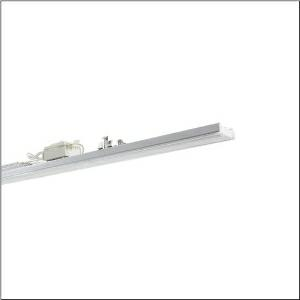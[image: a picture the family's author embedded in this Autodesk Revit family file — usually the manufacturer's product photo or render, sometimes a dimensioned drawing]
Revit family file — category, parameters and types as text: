
# Revit family: licross_r__21_recessed_ho_51te11vn4c5sd_75f8
name_source: partatom
category: Lighting Fixtures
units: mm (PartAtom-declared; Revit-internal decimal feet)

## family parameters
Cut with Voids When Loaded = No
Host = Face
Light Source = No
Part Type = Normal
Room Calculation Point = No
Round Connector Dimension = Use Diameter
Shared = No

## types (1)
- --- (1 x LED, 2050 lm, 12.3 W, 4000K)
    Apparent Load = 12 VA
    CIE Flux Codes = 84 94 98 99 100
    Color Rendering = 80
    Color Temperature = 4000K
    Default Elevation = 1800 mm
    Description = Licross® 21 Recessed HO, luminaire insert, of sheet steel, galvanised, coil coated, white, length: 1.500mm, width: 66mm, height: 67mm, LED rated luminous flux: 12.960lm, light colour: 840, control gear: DALI 2, CLO (for two DALI lines), with plug, 6-pole, with phase selection, mains connection: 220..240V, AC/DC, 0/50..60Hz, start of lifetime: 71W, end of service life: 77W, internal wiring halogen-free, for central battery installations according to DIN EN 60598-2-22, for emergency light function, without changeover relay, primary optical cover: cover, of PMMA, light emission: direct distribution, primary light characteristic: symmetric, protection rating (complete): IP54, insulation class (complete): insulation class I (protective earthing), certification: CE, ENEC, VDE, UKCA, protection symbol: D if used in an environment with non-conductive dust loads with corresponding accessories, impact resistance: IK06, permissible ambient temperature for indoor applications: -25..+35°C, standard: EN 60598-2-22, corresponds to IFS (International Featured Standards) requirements for safety and quality in the food industry, reducing of maximum allowable ambient temperature of 5°C with ceiling mounting, LABS conformity tested according to VDMA 24364:2018-05, packaging unit: 1 piece
    Height = 58 mm
    Lamp = 1 x LED
    Lamp Light Flux = 2050 lm
    Lamp Power = 12.3 W
    Lamp count = 1
    Length = 1500 mm
    Luminous efficacy = 167 lm/W
    Manufacturer = Siteco
    ModVariant = No
    Model = 51TE11VN4C5SD
    Mounting Place = Ceiling
    Mounting Type = Pendant
    Number of Poles = 1
    OnlyDefault = Yes
    Power Factor = 1
    Product Name = Licross® 21 Recessed HO
    Product group = luminaire insert | ceiling pendant
    ProductGroupID = 902
    Protection Class = Protection class I
    Protection Degree = IP 54
    RLX_Detail_Level = 1
    RLX_Emergency_Light_Flux = 0 lm
    RLX_Emergency_Type = 0
    RLX_Emergency_Type_DB = No
    RlxData = <blob elided: 25425 chars, md5=5d87726e>
    Socket = socket
    Standby Power = 0 W
    System Light Flux = 2050 lm
    System Power = 12 W
    Type Comments = : DC mode (central or group accumulator) initial emergency light level
    Type Image = l_1296930.jpg
    URL = http://relux.com
    VarID = @adj_069721
    Voltage = 0 V
    Weight = 0.00 kg
    Width = 66 mm

## geometry (parser evidence)
native form markers: Blend x4, Sweep x9
no freeform markers — native parametric forms only
